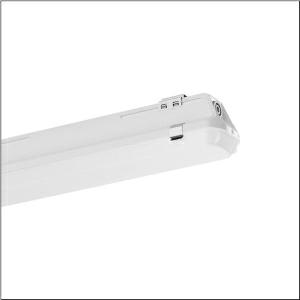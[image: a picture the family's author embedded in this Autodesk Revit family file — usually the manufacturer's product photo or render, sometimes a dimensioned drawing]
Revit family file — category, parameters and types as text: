
# Revit family: monsun_r__21_parking_51fg20dl430j_e9ef
name_source: partatom
category: Lighting Fixtures
units: mm (PartAtom-declared; Revit-internal decimal feet)

## family parameters
Cut with Voids When Loaded = No
Host = Face
Light Source = No
Part Type = Normal
Room Calculation Point = No
Round Connector Dimension = Use Diameter
Shared = No

## types (1)
- --- (1 x LED, 3850 lm, 26.4 W, 4000K)
    Apparent Load = 26 VA
    CIE Flux Codes = 45 75 93 94 100
    Color Rendering = 80
    Color Temperature = 4000K
    Default Elevation = 1800 mm
    Description = Monsun® 21 parking, damp-proof luminaire, chain hanger, primary optical cover: enclosure, of PC, light emission: direct distribution, primary light characteristic: symmetric, installation type: suspended mounting, surface-mounted, horizontal mounting, vertical mounting, LED, rated luminous flux: 3.850lm, luminous efficacy: 148lm/W, light colour: 840, colour temperature: 4000K, control gear: ECG DALI, with terminal, 5-pole, max. 2.5mm², mains connection: 220..240V, AC, 50/60Hz, rated input power: 26W, housing, of glass-fibre reinforced plastic, uncoated, bright grey, incl. chain hanger, length: 1.299mm, width: 90mm, height: 88mm, clip for enclosure, of stainless steel (V2A), ceiling mounting element, of stainless steel (V2A), chain hanger, of stainless steel (V2A), protection rating (complete): IP66, insulation class (complete): insulation class I (protective earthing), certification: CE, ENEC, VDE, UKCA, protection symbol: D, impact resistance: IK08, permissible operating ambient temperature: -25..+35°C, standard: EN 50419, EN 60598-2-1, corresponds to IFS (International Featured Standards) requirements for safety and quality in the food industry, for indoor or canopied outdoor use, no direct snow, no direct sun, no direct rain, contact your sales advisor before using the luminaires in applications with unclear chemical exposure, large temperature fluctuations or condensation-forming humidity, LABS conformity tested according to VDMA 24364:2018-05, packaging unit: 1 piece
    Height = 88 mm
    Lamp = 1 x LED
    Lamp Light Flux = 3850 lm
    Lamp Power = 26.4 W
    Lamp count = 1
    Length = 1299 mm
    Luminous efficacy = 146 lm/W
    Manufacturer = Siteco
    ModVariant = No
    Model = 51FG20DL430J
    Mounting Place = Ceiling
    Mounting Type = Surface mounted
    Number of Poles = 1
    OnlyDefault = Yes
    Power Factor = 1
    Product Name = Monsun® 21 parking
    Product group = damp-proof luminaire
    ProductGroupID = 300
    Protection Class = Protection class I
    Protection Degree = IP 66
    RLX_Detail_Level = 1
    RLX_Emergency_Light_Flux = 0 lm
    RLX_Emergency_Type = 0
    RLX_Emergency_Type_DB = No
    RlxData = <blob elided: 94013 chars, md5=3758d4f7>
    Socket = socket
    Standby Power = 0 W
    System Light Flux = 3850 lm
    System Power = 26 W
    Type Comments = factory setting: luminous flux: 100 % | dim-lin: 254 | 176 mA
    Type Image = l_1006717.jpg
    URL = http://relux.com
    VarID = @adj_077841
    Voltage = 0 V
    Weight = 0.00 kg
    Width = 90 mm

## geometry (parser evidence)
native form markers: Blend x4, Sweep x13
no freeform markers — native parametric forms only
